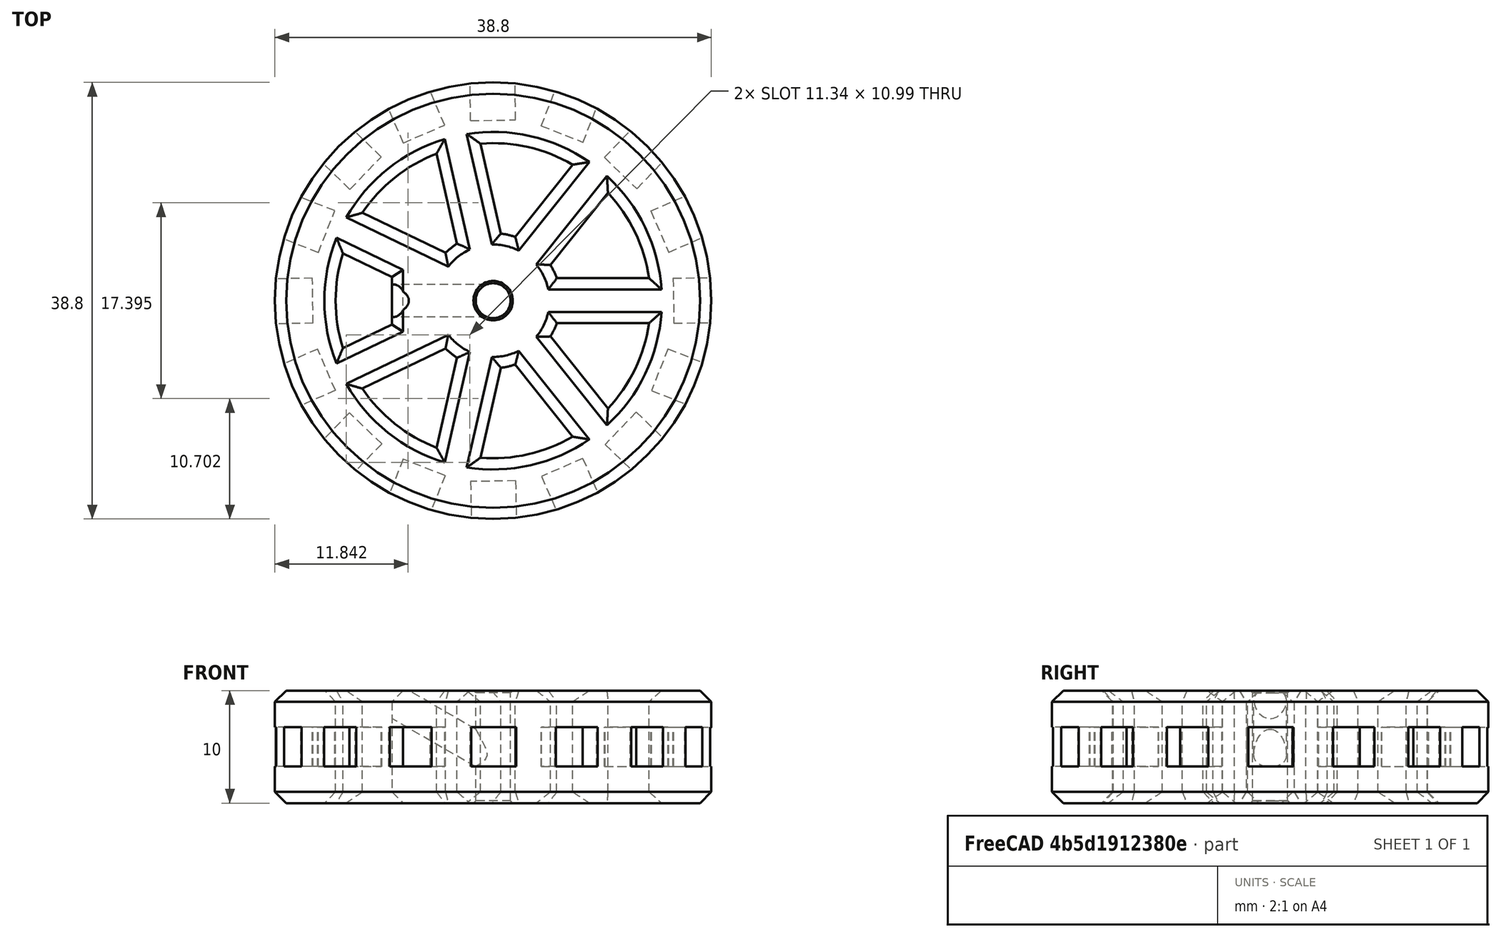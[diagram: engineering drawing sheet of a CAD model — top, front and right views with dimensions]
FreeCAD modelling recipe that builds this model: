
FCSTD DOCUMENT  (FreeCAD 0.17R13541 (Git))
Label: rueda16dientes
License: All rights reserved
LicenseURL: http://en.wikipedia.org/wiki/All_rights_reserved
objects: Part::Cylinder×5, Part::Box×3, Part::Chamfer×3, Part::MultiFuse×3, Part::FeaturePython×2, Part::Cut×2
note: 18 computed .brp shape members not serialized (recipe doc carries the construction recipe); baked Part::Feature solids carry a one-line shape summary decoded from their .brp

FEATURE [Part::Cylinder] Cylinder  label="Cilindro"
  Angle = 360
  AttacherType = Attacher::AttachEngine3D
  Height = 10
  Radius = 19.4
FEATURE [Part::Box] Box001  label="Cubo001"
  AttacherType = Attacher::AttachEngine3D
  Height = 3.5
  Length = 4
  Placement = pos=(-2,16,3.25) rot=(0,0,1;0.017453rad)
  Width = 10
FEATURE [Part::Cylinder] Cylinder001  label="Cilindro001"
  Angle = 360
  AttacherType = Attacher::AttachEngine3D
  Height = 10
  Radius = 14
FEATURE [Part::Cylinder] Cylinder002  label="eje"
  Angle = 360
  AttacherType = Attacher::AttachEngine3D
  Height = 20
  Radius = 1.55
FEATURE [Part::Cylinder] Cylinder003  label="buje"
  Angle = 360
  AttacherType = Attacher::AttachEngine3D
  Height = 10
  Radius = 6
FEATURE [Part::Box] Box002  label="Cubo002"
  AttacherType = Attacher::AttachEngine3D
  Height = 10
  Length = 10
  Placement = pos=(5,-2,0) rot=(0,0,1;0rad)
  Width = 4
FEATURE [Part::FeaturePython] Array001  # Draft array (typed FeaturePython)
  Angle = 360
  ArrayType = 1
  Axis = (0,0,1)
  Base = -> Box002
  Center = (0,0,0)
  Fuse = false
  IntervalAxis = (0,0,0)
  IntervalX = (1,0,0)
  IntervalY = (0,1,0)
  IntervalZ = (0,0,0)
  NumberPolar = 7
  NumberX = 2
  NumberY = 2
  NumberZ = 1
FEATURE [Part::Cylinder] Cylinder004  label="tornillo"
  Angle = 360
  AttacherType = Attacher::AttachEngine3D
  Height = 50
  Placement = pos=(0,0,4) rot=(0,-1,0;1.0472rad)
  Radius = 1.45
FEATURE [Part::Box] Box  label="Cubo"
  AttacherType = Attacher::AttachEngine3D
  Height = 10
  Length = 5
  Placement = pos=(-9,-4,0) rot=(0,0,1;0rad)
  Width = 8
FEATURE [Part::Chamfer] Chamfer001
  Base = -> Box
  Edges = 2 edges r=2: [Edge5,Edge7]
FEATURE [Part::FeaturePython] Array  # Draft array (typed FeaturePython)
  Angle = 360
  ArrayType = 1
  Axis = (0,0,1)
  Base = -> Box001
  Center = (0,0,0)
  Fuse = false
  IntervalAxis = (0,0,0)
  IntervalX = (1,0,0)
  IntervalY = (0,1,0)
  IntervalZ = (0,0,0)
  NumberPolar = 16
  NumberX = 2
  NumberY = 2
  NumberZ = 1
FEATURE [Part::Cut] Cut
  Base = -> Cylinder
  Refine = true
  Tool = -> Cylinder001
FEATURE [Part::MultiFuse] Fusion
  Refine = true
  Shapes = -> [Cut,Array001,Cylinder003]
FEATURE [Part::MultiFuse] Fusion001
  Refine = true
  Shapes = -> [Chamfer001,Fusion]
FEATURE [Part::Chamfer] Chamfer
  Base = -> Fusion001
  Edges = 58 edges r=1: [Edge1,Edge3,Edge4,Edge5,Edge6,Edge7,Edge8,Edge9,Edge10,Edge11,Edge12,Edge13,Edge14,Edge15,Edge16,Edge17,Edge18,Edge19,Edge20,Edge21,Edge22,Edge23,Edge24,Edge25,Edge26,Edge27,Edge28,Edge29,Edge30,Edge31,Edge33,Edge35,Edge37,Edge39,Edge41,Edge43,Edge45,Edge47,Edge49,Edge51,Edge53,Edge55,Edge57,Edge59,+14 more]
FEATURE [Part::MultiFuse] Fusion002
  Refine = true
  Shapes = -> [Cylinder004,Cylinder002,Array]
FEATURE [Part::Cut] Cut001
  Base = -> Chamfer
  Refine = true
  Tool = -> Fusion002
FEATURE [Part::Chamfer] Chamfer002
  Base = -> Cut001
  Edges = 2 edges r=0.2: [Edge211,Edge240]
